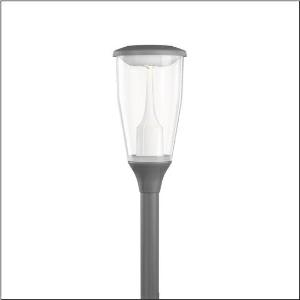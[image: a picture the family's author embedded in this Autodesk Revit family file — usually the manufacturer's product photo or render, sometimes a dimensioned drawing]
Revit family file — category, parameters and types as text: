
# Revit family: dl_11_iq___st1_2a_5xa5565ef14hp00022_07bc
name_source: partatom
category: Lighting Fixtures
units: mm (PartAtom-declared; Revit-internal decimal feet)

## family parameters
Cut with Voids When Loaded = No
Host = Face
Light Source = No
Part Type = Normal
Room Calculation Point = No
Round Connector Dimension = Use Diameter
Shared = No

## types (1)
- --- (1 x LED, 4840 lm, 33.6 W, 3000K)
    Apparent Load = 34 VA
    CIE Flux Codes = 33 63 91 94 100
    Color Rendering = 70
    Color Temperature = 3000K
    Default Elevation = 1800 mm
    Description = DL 11 iQ, mast luminaire, Module 540 iQ-SR, primary light control with 3 zone facetted reflector, of plastic, silver coated, highly specular, structured, primary optical cover: cover, of PMMA, transparent, light distribution: ST1.2a, light emission: direct distribution, primary light characteristic: asymmetric, installation type: post-top, LED, High Power LED, light colour: 730, colour temperature: 3000K, control: Street-Remote, Auto-Match, Temp-Guard, Lumen-Switch, Night-Set, Smart-Wire, Light-Fading, Desk-Remote (wireless, voltage-free reading and setting of iQ features in the workshop via application-optimized NFC function/RFID function), optimised constant luminous flux control (CLO 2.0), mains connection: 220..240V, AC, 50/60Hz, connection cable pre-assembled, cable length: 5,5m, start of lifetime: 34W, end of service life: 36W, luminaire housing, upper part, of diecast aluminium, coated, Siteco® metallic grey (DB 702S), spigot size: 60mm (post-top), post-top mast mounting element, of diecast aluminium, coated, Siteco® metallic grey (DB 702S), Module 540 iQ-SR, traffic white (RAL 9016), equipment: Power, protection rating (complete): IP66, insulation class (complete): insulation class II (safety insulation), certification: CE, ENEC, ENEC+, VDE, packaging unit: 1 piece

Light Distribution: ST1.2a
    Height = 665 mm
    Lamp = 1 x LED
    Lamp Light Flux = 4840 lm
    Lamp Power = 33.6 W
    Lamp count = 1
    Length = 334 mm
    Luminous efficacy = 144 lm/W
    Manufacturer = Siteco
    ModVariant = No
    Model = 5XA5565EF14HP00022
    Number of Poles = 1
    OnlyDefault = Yes
    Power Factor = 1
    Product Name = DL 11 iQ | ST1.2a
    Product group = mast luminaire | pylon top
    ProductGroupID = 6100
    Protection Class = Protection class II
    Protection Degree = IP 66
    RLX_Detail_Level = 1
    RLX_Emergency_Light_Flux = 0 lm
    RLX_Emergency_Type = 0
    RLX_Emergency_Type_DB = No
    RlxData = <blob elided: 97785 chars, md5=b969a0a8>
    Socket = socket
    Standby Power = 0 W
    System Light Flux = 4840 lm
    System Power = 34 W
    Type Comments = factory setting: luminous flux: 100 % | dim-lin: 254 | 695 mA
    Type Image = l_1258354.jpg
    URL = http://relux.com
    VarID = @adj_002689
    Voltage = 0 V
    Weight = 0.00 kg
    Width = 0 mm  [stored 0 ft]

note: [stored X ft] marks values corroborated as IEEE doubles in the binary element streams (Revit-internal decimal feet)

## geometry (parser evidence)
native form markers: Blend x4, Sweep x12
no freeform markers — native parametric forms only
